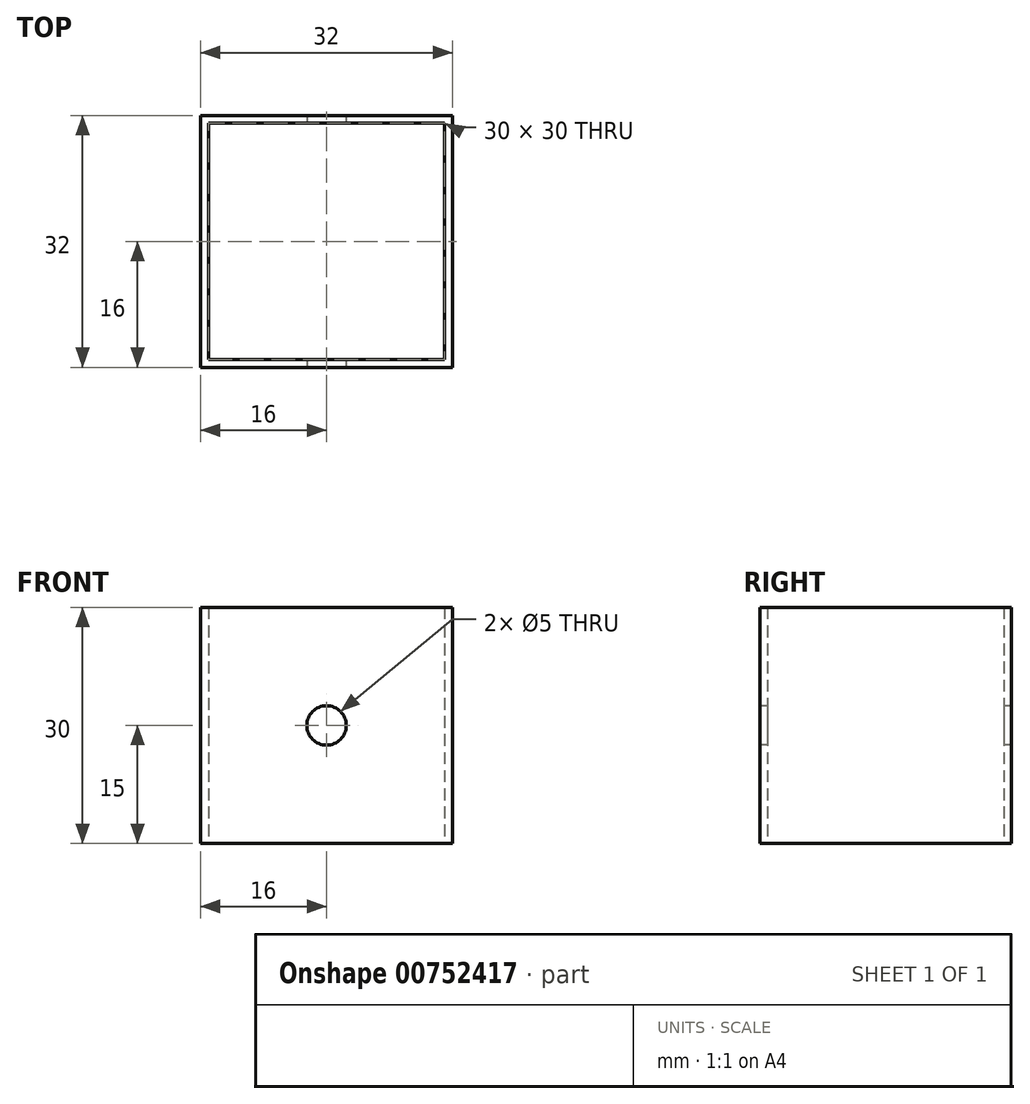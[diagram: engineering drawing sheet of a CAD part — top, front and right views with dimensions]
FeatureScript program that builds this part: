
annotation { "Feature Type Name" : "Feature", "Feature Type Description" : "" }
export const myFeature = defineFeature(function(context is Context, id is Id, definition is map)
    precondition{}
    {
        {
            var Q0;
            Q0=qCreatedBy(makeId("Top.planeOp"),FACE);
            var sketch = newSketch(context, id + "F0", { "sketchPlane" : qUnion([Q0])});
            skLineSegment(sketch, "E0.bottom", {"start": v(-15, 15) * mm, "end": v(15, 15) * mm});
            skLineSegment(sketch, "E0.top", {"start": v(-15, -15) * mm, "end": v(15, -15) * mm});
            skLineSegment(sketch, "E0.left", {"start": v(-15, 15) * mm, "end": v(-15, -15) * mm});
            skLineSegment(sketch, "E0.right", {"start": v(15, 15) * mm, "end": v(15, -15) * mm});
            skPoint(sketch, "E0.middle", {"position": v(0, 0) * mm});
            skPoint(sketch, "E1.middle", {"position": v(-19.97, 0) * mm});
            skPoint(sketch, "E1.left.end.orphan", {"position": v(-56.32, 37.65) * mm});
            skPoint(sketch, "E1.bottom.start.orphan", {"position": v(-56.32, -37.65) * mm});
            skPoint(sketch, "E1.right.end.orphan", {"position": v(16.4, 37.65) * mm});
            skPoint(sketch, "E1.right.start.orphan", {"position": v(16.4, -37.65) * mm});
            skLineSegment(sketch, "E2.bottom", {"start": v(-16, 16) * mm, "end": v(16, 16) * mm});
            skLineSegment(sketch, "E2.top", {"start": v(-16, -16) * mm, "end": v(16, -16) * mm});
            skLineSegment(sketch, "E2.left", {"start": v(-16, 16) * mm, "end": v(-16, -16) * mm});
            skLineSegment(sketch, "E2.right", {"start": v(16, 16) * mm, "end": v(16, -16) * mm});
            skSolve(sketch);
        }
        {
            var Q0;
            Q0 = qSketchRegion(id + "F0", true);
            extrude(context, id + "F1", {"entities" : qUnion([Q0]), "depth" : 30 * mm, "offsetDistance" : 25 * mm});
        }
        {
            var Q0;
            Q0=makeQuery(id+"F1.opExtrude","SWEPT_FACE",FACE,{"disambiguationData":[OSD([sQuery(id+"F0.wireOp",EDGE,"E2.top")])]});
            var sketch = newSketch(context, id + "F2", { "sketchPlane" : qUnion([Q0])});
            skCircle(sketch, "E3", {"center": v(0, 15) * mm, "radius": 2.5 * mm});
            skLineSegment(sketch, "E4", {"start": v(0, 0) * mm, "end": v(0, 15) * mm});
            skSolve(sketch);
        }
        {
            var Q0;
            Q0 = qSketchRegion(id + "F2", true);
            extrude(context, id + "F3", {"entities" : qUnion([Q0]), "operationType" : NewBodyOperationType.REMOVE, "oppositeDirection" : true, "depth" : 50 * mm, "offsetDistance" : 25 * mm});
        }
    });
